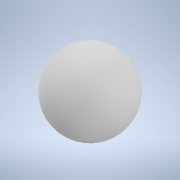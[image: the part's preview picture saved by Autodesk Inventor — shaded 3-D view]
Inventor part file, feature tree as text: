
AUTODESK INVENTOR PART (.ipt)
format: ipt  version: 2020 (Build 240168000, 168)  size: 121,344 bytes
history: native  units: in
note: dims shown in document units (in); Inventor stores cm internally (conversion verified against a paired STEP export)
features: revolve x1, sketch x1
ambient origin geometry x8: Origin, YZ Plane, XZ Plane, XY Plane, X Axis, Y Axis, Z Axis, Center Point
bodies: Solid1 (feature_tree)
feature tree (2):
  revolve  "Revolution1"  [1 undecoded]
  sketch  "Sketch1"  dims[d1=5.0in d2=2.6in d3=360.0deg]
note: 1 required parameter value undecoded (feature->parameter linkage not recoverable at this tier; creation-order binding heuristic only, values carry confidence <= 0.55)
